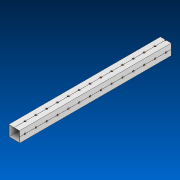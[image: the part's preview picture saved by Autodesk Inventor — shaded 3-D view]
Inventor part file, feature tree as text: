
AUTODESK INVENTOR PART (.ipt)
format: ipt  version: 2022.2 (Build 262287000, 287)  size: 766,976 bytes
history: native  units: in
note: dims shown in document units (in); Inventor stores cm internally (conversion verified against a paired STEP export)
features: other x28, pattern_linear x2, extrude x1, sketch x1
ambient origin geometry x8: Origin, YZ Plane, XZ Plane, XY Plane, X Axis, Y Axis, Z Axis, Center Point
bodies: Solid1 (feature_tree)
feature tree (32):
  extrude  "Extrusion1"  TaperAngle=0.0deg  [1 undecoded]
  other  "Work Axis1"
  other  "Work Axis2"
  pattern_linear  "Rectangular Pattern1"  Count1=14  [1 undecoded]
  pattern_linear  "Rectangular Pattern2"  Spacing1=1.0in  [1 undecoded]
  sketch  "Sketch1"  dims[d0=45.0in d1=0.0in d2=5.5118in d4=1.0in d5=5.1181in d7=1.0in]
  other  "Work Axis3"
  other  "Work Axis4"
  other  "Work Axis5"
  other  "Work Axis6"
  other  "Work Axis7"
  other  "Work Axis8"
  other  "Work Axis9"
  other  "Work Axis10"
  other  "Work Axis11"
  other  "Work Axis12"
  other  "Work Axis13"
  other  "Work Axis14"
  other  "Work Axis15"
  other  "Work Axis16"
  other  "Work Axis17"
  other  "Work Axis63"
  other  "Work Axis64"
  other  "Work Axis65"
  other  "Work Axis66"
  other  "Work Axis67"
  other  "Work Axis68"
  other  "Work Axis69"
  other  "Work Axis70"
  other  "Work Axis71"
  other  "Work Axis72"
  other  "LPattern2"
note: 3 required parameter values undecoded (feature->parameter linkage not recoverable at this tier; creation-order binding heuristic only, values carry confidence <= 0.55)
